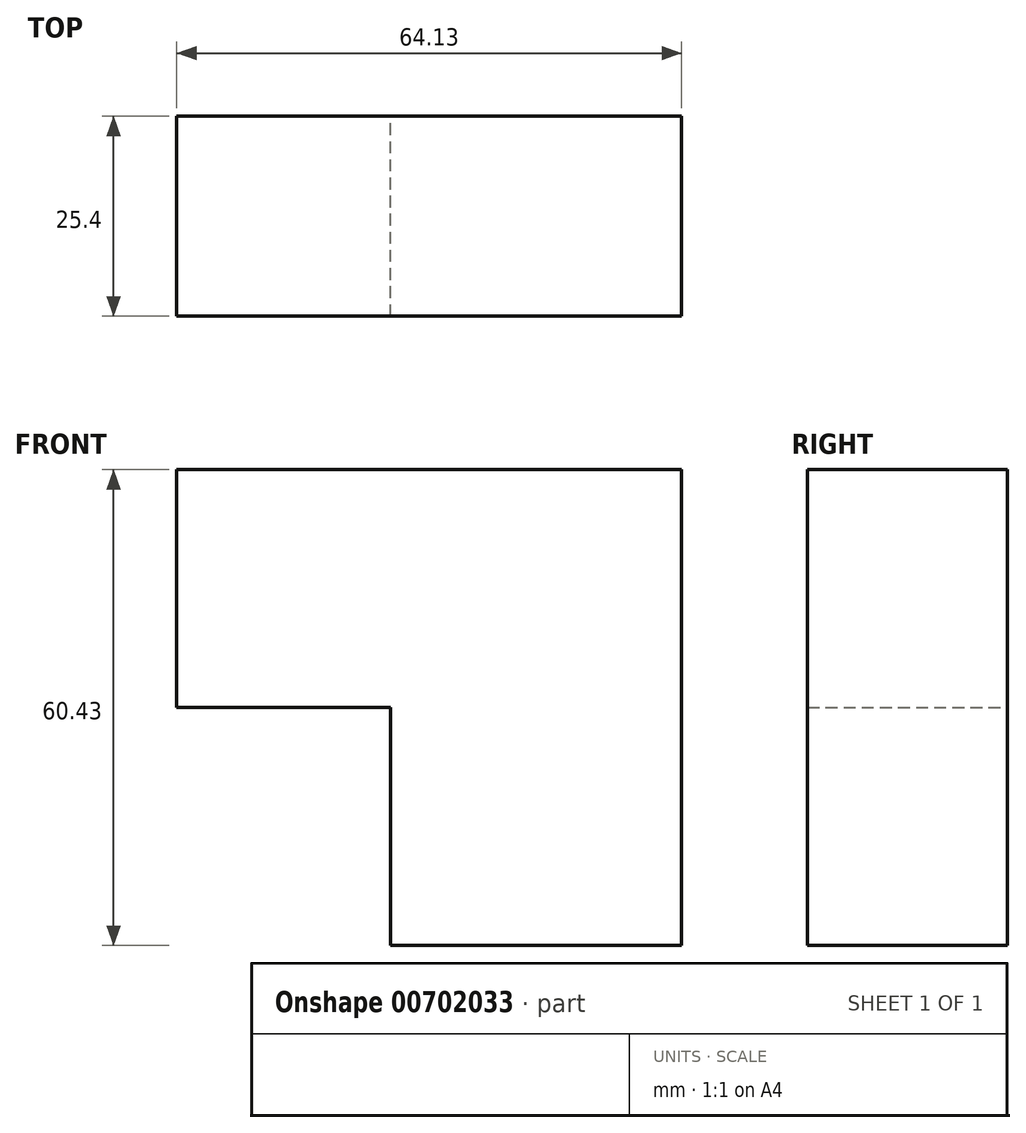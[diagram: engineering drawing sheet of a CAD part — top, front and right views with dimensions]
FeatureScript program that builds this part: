
annotation { "Feature Type Name" : "Feature", "Feature Type Description" : "" }
export const myFeature = defineFeature(function(context is Context, id is Id, definition is map)
    precondition{}
    {
        {
            var Q0;
            Q0=qCreatedBy(makeId("Front.planeOp"),FACE);
            var sketch = newSketch(context, id + "F0", { "sketchPlane" : qUnion([Q0])});
            skLineSegment(sketch, "E0.bottom", {"start": v(-20.14, 30.42) * mm, "end": v(43.99, 30.42) * mm});
            skLineSegment(sketch, "E0.top", {"start": v(-20.14, -30.01) * mm, "end": v(43.99, -30.01) * mm});
            skLineSegment(sketch, "E0.left", {"start": v(-20.14, 30.42) * mm, "end": v(-20.14, -30.01) * mm});
            skLineSegment(sketch, "E0.right", {"start": v(43.99, 30.42) * mm, "end": v(43.99, -30.01) * mm});
            skLineSegment(sketch, "E1.bottom", {"start": v(-20.14, 0.2) * mm, "end": v(7, 0.2) * mm});
            skLineSegment(sketch, "E1.top", {"start": v(-20.14, -30.01) * mm, "end": v(7, -30.01) * mm});
            skLineSegment(sketch, "E1.left", {"start": v(-20.14, 0.2) * mm, "end": v(-20.14, -30.01) * mm});
            skLineSegment(sketch, "E1.right", {"start": v(7, 0.2) * mm, "end": v(7, -30.01) * mm});
            skSolve(sketch);
        }
        {
            var Q0;
            Q0=makeQuery(id+"F0.imprint","IMPRINT",FACE,{"disambiguationData":[TD([[makeQuery(id+"F0.imprint","IMPRINT",EDGE,{"derivedFrom":sQuery(id+"F0.wireOp",EDGE,"E0.bottom")}),-1.0]])]});
            extrude(context, id + "F1", {"entities" : qUnion([Q0]), "depth" : 25.4 * mm, "offsetDistance" : 25.4 * mm});
        }
    });
